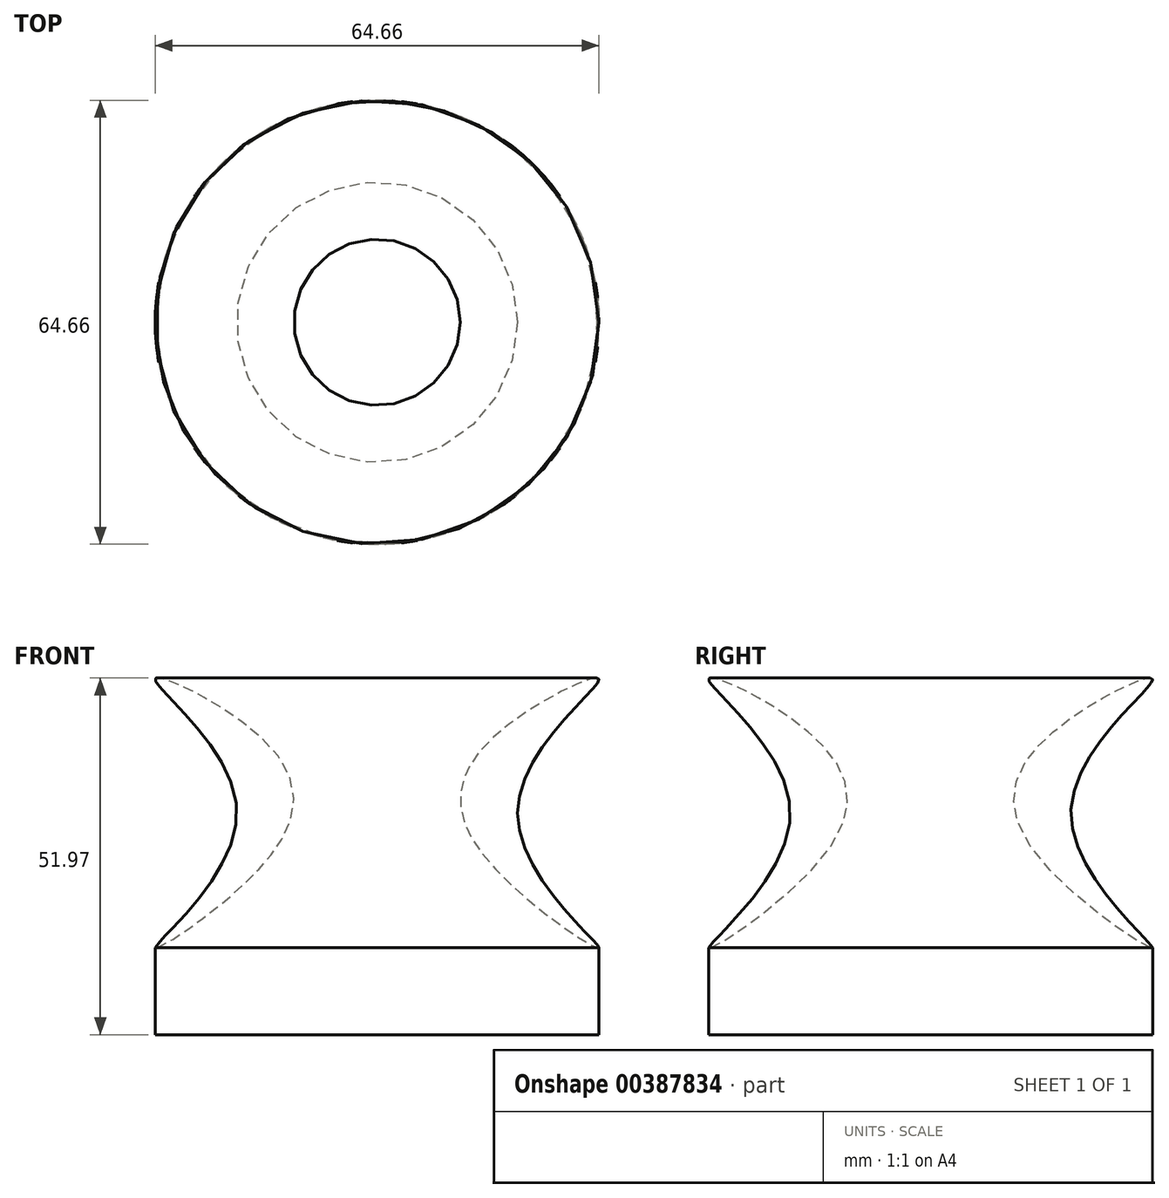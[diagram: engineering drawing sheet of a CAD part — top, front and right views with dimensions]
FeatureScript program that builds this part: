
annotation { "Feature Type Name" : "Feature", "Feature Type Description" : "" }
export const myFeature = defineFeature(function(context is Context, id is Id, definition is map)
    precondition{}
    {
        {
            var Q0;
            Q0=qCreatedBy(makeId("Front.planeOp"),FACE);
            var sketch = newSketch(context, id + "F0", { "sketchPlane" : qUnion([Q0])});
            skLineSegment(sketch, "E0", {"start": v(0, 0) * mm, "end": v(0, 12.65) * mm});
            skLineSegment(sketch, "E1", {"start": v(0, 12.65) * mm, "end": v(32.33, 12.65) * mm});
            skLineSegment(sketch, "E2", {"start": v(32.33, 12.65) * mm, "end": v(32.33, 0) * mm});
            skLineSegment(sketch, "E3", {"start": v(32.33, 0) * mm, "end": v(0, 0) * mm});
            skFitSpline(sketch, "E4", {"points": [v(32.33, 12.65) * mm, v(20.44, 32.37) * mm, v(32.33, 51.8) * mm, v(16.39, 42.8) * mm, v(14.94, 26.86) * mm, v(32.33, 12.65) * mm]});
            skLineSegment(sketch, "E5", {"start": v(0, 41.36) * mm, "end": v(0, 0) * mm});
            skSolve(sketch);
        }
        {
            var Q0;
            Q0 = qSketchRegion(id + "F0", true);
            var Q1;
            Q1=sQuery(id+"F0.wireOp",EDGE,"E5");
            revolve(context, id + "F1", {"entities" : qUnion([Q0]), "axis" : qUnion([Q1]), "revolveType" : RevolveType.FULL});
        }
    });
